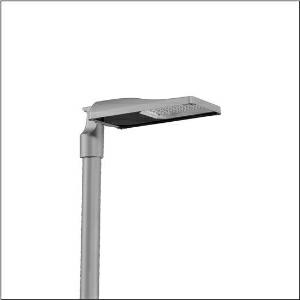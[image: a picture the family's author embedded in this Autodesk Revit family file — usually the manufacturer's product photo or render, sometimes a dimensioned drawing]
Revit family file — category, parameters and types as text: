
# Revit family: streetlight_sl_31_mini___st1_0a_5xh6d3ab08ha_9874
name_source: partatom
category: Lighting Fixtures
units: mm (PartAtom-declared; Revit-internal decimal feet)

## family parameters
Cut with Voids When Loaded = No
Host = Face
Light Source = No
Part Type = Normal
Room Calculation Point = No
Round Connector Dimension = Use Diameter
Shared = No

## types (1)
- --- (1 x LED, 9240 lm, 68.3 W, 3000K)
    Apparent Load = 68 VA
    CIE Flux Codes = 37 72 97 100 100
    Color Rendering = 70
    Color Temperature = 3000K
    Default Elevation = 1800 mm
    Description = Streetlight SL 31 mini Easy LST mast luminaire for post-top, side-entry; light control with lens of PMMA; light distribution: ST1.0a, direct asymmetric distribution, for standard-compliant lighting for roads and squares; LED: luminous flux: 9.240lm, light colour: 730, colour temperature: 3000K; luminous efficacy: 135,3lm/W; control: pre-setting: linear dimming characteristic, flexible luminous flux parameterisation, time-dependent luminous flux control, constant luminous flux control, power reduction, intelligent temperature release in ECG and LED module, overheat protection; luminaire housing, of diecast aluminium, Siteco® metallic grey (DB 702S), corrosivity category C5 high according to DIN EN ISO 12944; cover of toughened safety glass, transparent, opened without tools; mast flange of diecast aluminium, Siteco® metallic grey (DB 702S), spigot size: 76/60mm, mast flange included unmounted; with cable H07RN-F 3x 1.5mm², cable length: 8,5m, connection cable pre-assembled; mains connection: 220..240V, AC, 50/60Hz; power consumption (at start of service life): 68,3W / (at end of service life): 74,8W / (with reduced operation 50%): 29,7W; protection rating (complete): IP66; insulation class (complete): insulation class II (safety insulation); impact resistance: IK10; certification: CE, ENEC, ENEC+, VDE, UKCA; permissible operating ambient temperature for outdoor applications: -40..+50°C; packaging unit: 1 piece

Light Distribution: ST1.0a
    Height = 76 mm
    Lamp = 1 x LED
    Lamp Light Flux = 9240 lm
    Lamp Power = 68.3 W
    Lamp count = 1
    Length = 547 mm
    Luminous efficacy = 135 lm/W
    Manufacturer = Siteco
    ModVariant = No
    Model = 5XH6D3AB08HA
    Number of Poles = 1
    OnlyDefault = Yes
    Power Factor = 1
    Product Name = Streetlight SL 31 mini | ST1.0a
    Product group = mast luminaire | pylon top
    ProductGroupID = 6100
    Protection Class = Protection class II
    Protection Degree = IP 66
    RLX_Detail_Level = 1
    RLX_Emergency_Light_Flux = 0 lm
    RLX_Emergency_Type = 0
    RLX_Emergency_Type_DB = No
    RlxData = <blob elided: 39361 chars, md5=d7a02702>
    Socket = socket
    Standby Power = 0 W
    System Light Flux = 9240 lm
    System Power = 68 W
    Type Comments = factory setting: luminous flux: 100 % | dim-lin: 254 | 693 mA
    Type Image = l_1300326.jpg
    URL = http://relux.com
    VarID = @adj_074507
    Voltage = 0 V
    Weight = 0.00 kg
    Width = 265 mm

## geometry (parser evidence)
native form markers: Blend x4, Sweep x9
no freeform markers — native parametric forms only
